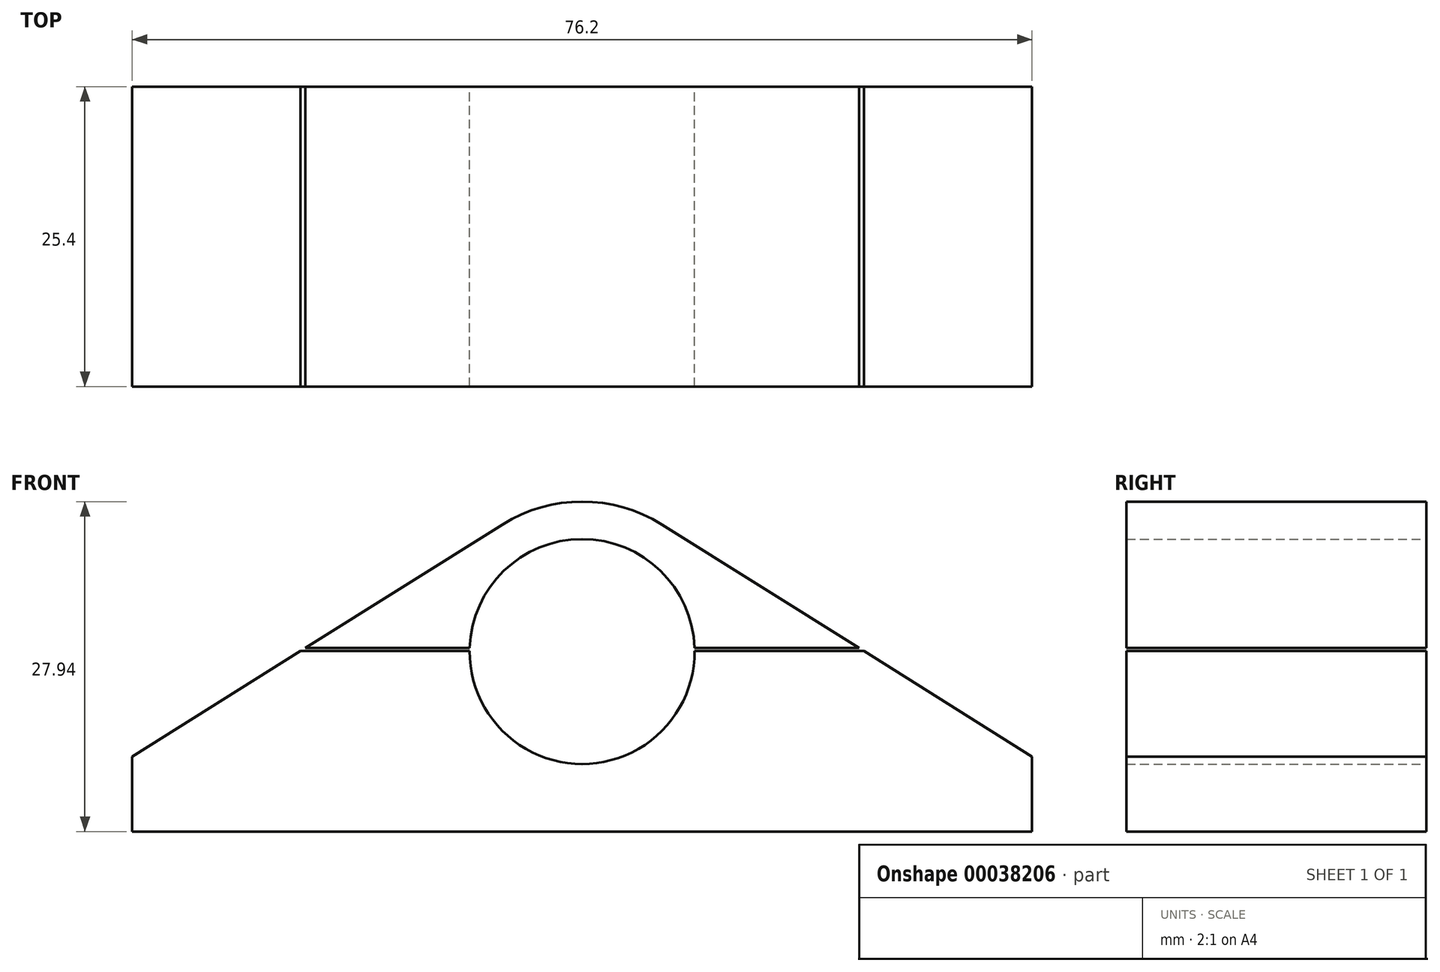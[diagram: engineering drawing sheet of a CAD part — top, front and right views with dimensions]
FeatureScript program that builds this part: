
annotation { "Feature Type Name" : "Feature", "Feature Type Description" : "" }
export const myFeature = defineFeature(function(context is Context, id is Id, definition is map)
    precondition{}
    {
        {
            var Q0;
            Q0=qCreatedBy(makeId("Top.planeOp"),FACE);
            var sketch = newSketch(context, id + "F0", { "sketchPlane" : qUnion([Q0])});
            skLineSegment(sketch, "E0.bottom", {"start": v(-38.1, 12.7) * mm, "end": v(38.1, 12.7) * mm});
            skLineSegment(sketch, "E0.top", {"start": v(-38.1, -12.7) * mm, "end": v(38.1, -12.7) * mm});
            skLineSegment(sketch, "E0.left", {"start": v(-38.1, 12.7) * mm, "end": v(-38.1, -12.7) * mm});
            skLineSegment(sketch, "E0.right", {"start": v(38.1, 12.7) * mm, "end": v(38.1, -12.7) * mm});
            skSolve(sketch);
        }
        {
            var Q0;
            Q0=makeQuery(id+"F0.imprint","IMPRINT",FACE,{"disambiguationData":[TD([[makeQuery(id+"F0.imprint","IMPRINT",EDGE,{"derivedFrom":sQuery(id+"F0.wireOp",EDGE,"E0.bottom")}),-1.0]])]});
            extrude(context, id + "F1", {"entities" : qUnion([Q0]), "depth" : 6.35 * mm});
        }
        {
            var Q0;
            Q0=makeQuery(id+"F1.opExtrude","SWEPT_FACE",FACE,{"disambiguationData":[OSD([sQuery(id+"F0.wireOp",EDGE,"E0.bottom")])]});
            var sketch = newSketch(context, id + "F2", { "sketchPlane" : qUnion([Q0])});
            skCircle(sketch, "E1", {"center": v(0, 15.24) * mm, "radius": 9.53 * mm});
            skLineSegment(sketch, "E2", {"start": v(-38.1, 6.35) * mm, "end": v(-6.74, 26) * mm});
            skLineSegment(sketch, "E3", {"start": v(38.1, 6.35) * mm, "end": v(6.74, 26) * mm});
            skLineSegment(sketch, "E4", {"start": v(-38.1, 6.35) * mm, "end": v(-3.42, 6.35) * mm});
            skArc(sketch, "E5.trimOffspring", {"start": v(6.74, 26) * mm, "mid": v(0, 27.94) * mm, "end": v(-6.74, 26) * mm});
            skLineSegment(sketch, "E6.trimOffspring", {"start": v(3.42, 6.35) * mm, "end": v(38.1, 6.35) * mm});
            skSolve(sketch);
        }
        {
            var Q0;
            Q0=makeQuery(id+"F2.imprint","IMPRINT",FACE,{"disambiguationData":[TD([[makeQuery(id+"F2.imprint","IMPRINT",EDGE,{"derivedFrom":sQuery(id+"F2.wireOp",EDGE,"E2")}),-1.0]])]});
            var Q1;
            {var subQ0=makeQuery(id+"F1.opExtrude","CAP_EDGE",EDGE,{"disambiguationData":[OSD([sQuery(id+"F0.wireOp",EDGE,"E0.bottom")])],"isStart":false});var subQ1=sQuery(id+"F2.wireOp",EDGE,"E1");var subQ3=makeQuery(id+"F2.imprint","INTERSECT",VERTEX,{"derivedFrom":[subQ0,subQ1,sQuery(id+"F2.wireOp",EDGE,"E4")]});Q1=makeQuery(id+"F2.imprint","IMPRINT",FACE,{"disambiguationData":[TD([[makeQuery(id+"F2.imprint","IMPRINT",EDGE,{"disambiguationData":[TD([[subQ3,-1.0]])],"derivedFrom":subQ1}),1.0]])]});}
            var Q2;
            Q2=makeQuery(id+"F1.opExtrude","SWEPT_FACE",FACE,{"disambiguationData":[OSD([sQuery(id+"F0.wireOp",EDGE,"E0.top")])]});
            extrude(context, id + "F3", {"entities" : qUnion([Q0, Q1]), "operationType" : NewBodyOperationType.ADD, "endBound" : BoundingType.UP_TO_SURFACE, "oppositeDirection" : true, "endBoundEntityFace" : qUnion([Q2]), "depth" : 20.8 * mm});
        }
        {
            var Q0;
            Q0=makeQuery(id+"F3.boolean.opBoolean","MERGE",FACE,{"derivedFrom":[makeQuery(id+"F1.opExtrude","SWEPT_FACE",FACE,{"disambiguationData":[OSD([sQuery(id+"F0.wireOp",EDGE,"E0.bottom")])]}),makeQuery(id+"F3.opExtrude","CAP_FACE",FACE,{"disambiguationData":[OSD([sQuery(id+"F2.wireOp",EDGE,"E1"),sQuery(id+"F2.wireOp",EDGE,"E2"),sQuery(id+"F2.wireOp",EDGE,"E3"),sQuery(id+"F2.wireOp",EDGE,"E4"),sQuery(id+"F2.wireOp",EDGE,"E5.trimOffspring"),sQuery(id+"F2.wireOp",EDGE,"E6.trimOffspring")])],"isStart":true})]});
            var sketch = newSketch(context, id + "F4", { "sketchPlane" : qUnion([Q0])});
            skCircle(sketch, "E7", {"center": v(0, 15.24) * mm, "radius": 9.53 * mm});
            skSolve(sketch);
        }
        {
            var Q0;
            Q0 = qSketchRegion(id + "F4", true);
            var Q1;
            Q1=makeQuery(id+"F3.boolean.opBoolean","MERGE",FACE,{"derivedFrom":[makeQuery(id+"F1.opExtrude","SWEPT_FACE",FACE,{"disambiguationData":[OSD([sQuery(id+"F0.wireOp",EDGE,"E0.top")])]}),makeQuery(id+"F3.opExtrude","CAP_FACE",FACE,{"disambiguationData":[OSD([sQuery(id+"F2.wireOp",EDGE,"E1"),sQuery(id+"F2.wireOp",EDGE,"E2"),sQuery(id+"F2.wireOp",EDGE,"E3"),sQuery(id+"F2.wireOp",EDGE,"E4"),sQuery(id+"F2.wireOp",EDGE,"E5.trimOffspring"),sQuery(id+"F2.wireOp",EDGE,"E6.trimOffspring")])],"isStart":false})]});
            extrude(context, id + "F5", {"entities" : qUnion([Q0]), "operationType" : NewBodyOperationType.REMOVE, "endBound" : BoundingType.UP_TO_SURFACE, "oppositeDirection" : true, "endBoundEntityFace" : qUnion([Q1]), "depth" : 25.4 * mm});
        }
        {
            var Q0;
            Q0=makeQuery(id+"F3.boolean.opBoolean","MERGE",FACE,{"derivedFrom":[makeQuery(id+"F1.opExtrude","SWEPT_FACE",FACE,{"disambiguationData":[OSD([sQuery(id+"F0.wireOp",EDGE,"E0.bottom")])]}),makeQuery(id+"F3.opExtrude","CAP_FACE",FACE,{"disambiguationData":[OSD([sQuery(id+"F2.wireOp",EDGE,"E1"),sQuery(id+"F2.wireOp",EDGE,"E2"),sQuery(id+"F2.wireOp",EDGE,"E3"),sQuery(id+"F2.wireOp",EDGE,"E4"),sQuery(id+"F2.wireOp",EDGE,"E5.trimOffspring"),sQuery(id+"F2.wireOp",EDGE,"E6.trimOffspring")])],"isStart":true})]});
            var sketch = newSketch(context, id + "F6", { "sketchPlane" : qUnion([Q0])});
            skLineSegment(sketch, "E8", {"start": v(-23.45, 15.53) * mm, "end": v(23.45, 15.53) * mm});
            skLineSegment(sketch, "E9.0", {"start": v(-23.85, 15.28) * mm, "end": v(23.85, 15.28) * mm});
            skLineSegment(sketch, "E10", {"start": v(23.85, 15.28) * mm, "end": v(23.45, 15.53) * mm});
            skLineSegment(sketch, "E11", {"start": v(-23.45, 15.53) * mm, "end": v(-23.85, 15.28) * mm});
            skSolve(sketch);
        }
        {
            var Q0;
            {var subQ6=sQuery(id+"F6.wireOp",EDGE,"E10");Q0=makeQuery(id+"F6.imprint","IMPRINT",FACE,{"disambiguationData":[TD([[makeQuery(id+"F6.imprint","IMPRINT",EDGE,{"derivedFrom":subQ6}),1.0]])]});}
            var Q1;
            {var subQ7=sQuery(id+"F6.wireOp",EDGE,"E11");Q1=makeQuery(id+"F6.imprint","IMPRINT",FACE,{"disambiguationData":[TD([[makeQuery(id+"F6.imprint","IMPRINT",EDGE,{"derivedFrom":subQ7}),-1.0]])]});}
            var Q2;
            Q2=makeQuery(id+"F3.boolean.opBoolean","MERGE",FACE,{"derivedFrom":[makeQuery(id+"F1.opExtrude","SWEPT_FACE",FACE,{"disambiguationData":[OSD([sQuery(id+"F0.wireOp",EDGE,"E0.top")])]}),makeQuery(id+"F3.opExtrude","CAP_FACE",FACE,{"disambiguationData":[OSD([sQuery(id+"F2.wireOp",EDGE,"E1"),sQuery(id+"F2.wireOp",EDGE,"E2"),sQuery(id+"F2.wireOp",EDGE,"E3"),sQuery(id+"F2.wireOp",EDGE,"E4"),sQuery(id+"F2.wireOp",EDGE,"E5.trimOffspring"),sQuery(id+"F2.wireOp",EDGE,"E6.trimOffspring")])],"isStart":false})]});
            extrude(context, id + "F7", {"entities" : qUnion([Q0, Q1]), "operationType" : NewBodyOperationType.REMOVE, "endBound" : BoundingType.UP_TO_SURFACE, "oppositeDirection" : true, "endBoundEntityFace" : qUnion([Q2]), "depth" : 25.4 * mm});
        }
    });
